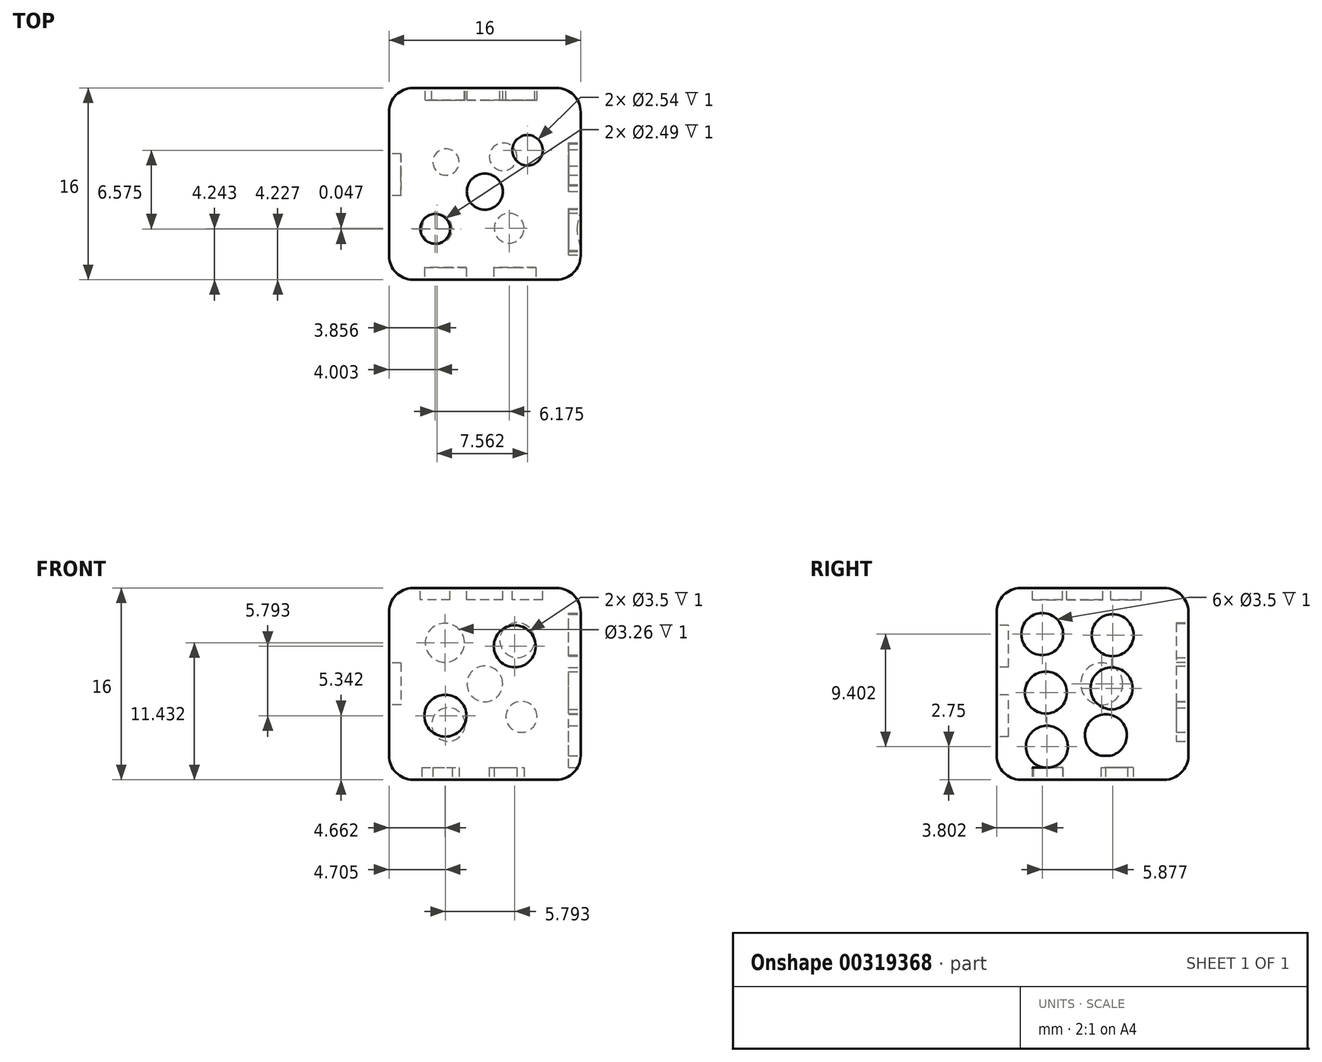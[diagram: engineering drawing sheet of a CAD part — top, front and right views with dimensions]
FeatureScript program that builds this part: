
annotation { "Feature Type Name" : "Feature", "Feature Type Description" : "" }
export const myFeature = defineFeature(function(context is Context, id is Id, definition is map)
    precondition{}
    {
        {
            var Q0;
            Q0=qCreatedBy(makeId("Front.planeOp"),FACE);
            var sketch = newSketch(context, id + "F0", { "sketchPlane" : qUnion([Q0])});
            skLineSegment(sketch, "E0.bottom", {"start": v(8, 8) * mm, "end": v(-8, 8) * mm});
            skLineSegment(sketch, "E0.top", {"start": v(8, -8) * mm, "end": v(-8, -8) * mm});
            skLineSegment(sketch, "E0.left", {"start": v(8, 8) * mm, "end": v(8, -8) * mm});
            skLineSegment(sketch, "E0.right", {"start": v(-8, 8) * mm, "end": v(-8, -8) * mm});
            skPoint(sketch, "E0.middle", {"position": v(0, 0) * mm});
            skSolve(sketch);
        }
        {
            var Q0;
            Q0 = qSketchRegion(id + "F0", true);
            extrude(context, id + "F1", {"entities" : qUnion([Q0]), "depth" : 16 * mm});
        }
        {
            var Q0;
            Q0=makeQuery(id+"F1.opExtrude","CAP_EDGE",EDGE,{"disambiguationData":[OSD([sQuery(id+"F0.wireOp",EDGE,"E0.left")])],"isStart":false});
            var Q1;
            Q1=makeQuery(id+"F1.opExtrude","CAP_EDGE",EDGE,{"disambiguationData":[OSD([sQuery(id+"F0.wireOp",EDGE,"E0.bottom")])],"isStart":false});
            var Q2;
            Q2=makeQuery(id+"F1.opExtrude","CAP_EDGE",EDGE,{"disambiguationData":[OSD([sQuery(id+"F0.wireOp",EDGE,"E0.top")])],"isStart":false});
            var Q3;
            Q3=makeQuery(id+"F1.opExtrude","CAP_EDGE",EDGE,{"disambiguationData":[OSD([sQuery(id+"F0.wireOp",EDGE,"E0.right")])],"isStart":false});
            var Q4;
            Q4=makeQuery(id+"F1.opExtrude","CAP_EDGE",EDGE,{"disambiguationData":[OSD([sQuery(id+"F0.wireOp",EDGE,"E0.right")])],"isStart":true});
            var Q5;
            Q5=makeQuery(id+"F1.opExtrude","SWEPT_EDGE",EDGE,{"disambiguationData":[OSD([sQuery(id+"F0.wireOp",EDGE,"E0.bottom"),sQuery(id+"F0.wireOp",EDGE,"E0.right")])]});
            var Q6;
            Q6=makeQuery(id+"F1.opExtrude","SWEPT_EDGE",EDGE,{"disambiguationData":[OSD([sQuery(id+"F0.wireOp",EDGE,"E0.top"),sQuery(id+"F0.wireOp",EDGE,"E0.right")])]});
            var Q7;
            Q7=makeQuery(id+"F1.opExtrude","SWEPT_FACE",FACE,{"disambiguationData":[OSD([sQuery(id+"F0.wireOp",EDGE,"E0.right")])]});
            var Q8;
            Q8=makeQuery(id+"F1.opExtrude","CAP_EDGE",EDGE,{"disambiguationData":[OSD([sQuery(id+"F0.wireOp",EDGE,"E0.bottom")])],"isStart":true});
            var Q9;
            Q9=makeQuery(id+"F1.opExtrude","SWEPT_EDGE",EDGE,{"disambiguationData":[OSD([sQuery(id+"F0.wireOp",EDGE,"E0.bottom"),sQuery(id+"F0.wireOp",EDGE,"E0.left")])]});
            var Q10;
            Q10=makeQuery(id+"F1.opExtrude","CAP_EDGE",EDGE,{"disambiguationData":[OSD([sQuery(id+"F0.wireOp",EDGE,"E0.left")])],"isStart":true});
            var Q11;
            Q11=makeQuery(id+"F1.opExtrude","CAP_EDGE",EDGE,{"disambiguationData":[OSD([sQuery(id+"F0.wireOp",EDGE,"E0.top")])],"isStart":true});
            var Q12;
            Q12=makeQuery(id+"F1.opExtrude","SWEPT_EDGE",EDGE,{"disambiguationData":[OSD([sQuery(id+"F0.wireOp",EDGE,"E0.top"),sQuery(id+"F0.wireOp",EDGE,"E0.left")])]});
            fillet(context, id + "F2", {"entities" : qUnion([Q0, Q1, Q2, Q3, Q4, Q5, Q6, Q7, Q8, Q9, Q10, Q11, Q12]), "radius" : 2 * mm, "tangentPropagation" : true, "allowEdgeOverflow" : false});
        }
        {
            var Q0;
            Q0=makeQuery(id+"F1.opExtrude","CAP_FACE",FACE,{"disambiguationData":[OSD([sQuery(id+"F0.wireOp",EDGE,"E0.bottom"),sQuery(id+"F0.wireOp",EDGE,"E0.top"),sQuery(id+"F0.wireOp",EDGE,"E0.left"),sQuery(id+"F0.wireOp",EDGE,"E0.right")])],"isStart":false});
            var sketch = newSketch(context, id + "F3", { "sketchPlane" : qUnion([Q0])});
            skCircle(sketch, "E1", {"center": v(-3.3, -2.66) * mm, "radius": 1.75 * mm});
            skCircle(sketch, "E2", {"center": v(2.5, 3.14) * mm, "radius": 1.75 * mm});
            skSolve(sketch);
        }
        {
            var Q0;
            Q0=makeQuery(id+"F1.opExtrude","SWEPT_FACE",FACE,{"disambiguationData":[OSD([sQuery(id+"F0.wireOp",EDGE,"E0.right")])]});
            var sketch = newSketch(context, id + "F4", { "sketchPlane" : qUnion([Q0])});
            skCircle(sketch, "E3", {"center": v(7.24, 0) * mm, "radius": 1.75 * mm});
            skPoint(sketch, "E3.centerSnap0", {"position": v(2, 0) * mm});
            skSolve(sketch);
        }
        {
            var Q0;
            Q0=makeQuery(id+"F1.opExtrude","CAP_FACE",FACE,{"disambiguationData":[OSD([sQuery(id+"F0.wireOp",EDGE,"E0.bottom"),sQuery(id+"F0.wireOp",EDGE,"E0.top"),sQuery(id+"F0.wireOp",EDGE,"E0.left"),sQuery(id+"F0.wireOp",EDGE,"E0.right")])],"isStart":true});
            var sketch = newSketch(context, id + "F5", { "sketchPlane" : qUnion([Q0])});
            skCircle(sketch, "E4", {"center": v(0, 0) * mm, "radius": 1.5 * mm});
            skCircle(sketch, "E5", {"center": v(3.05, -3.4) * mm, "radius": 1.4 * mm});
            skCircle(sketch, "E6", {"center": v(-2.7, 3.65) * mm, "radius": 1.46 * mm});
            skCircle(sketch, "E7", {"center": v(3.34, 3.43) * mm, "radius": 1.63 * mm});
            skCircle(sketch, "E8", {"center": v(-3.06, -2.75) * mm, "radius": 1.3 * mm});
            skSolve(sketch);
        }
        {
            var Q0;
            Q0=makeQuery(id+"F1.opExtrude","SWEPT_FACE",FACE,{"disambiguationData":[OSD([sQuery(id+"F0.wireOp",EDGE,"E0.bottom")])]});
            var sketch = newSketch(context, id + "F6", { "sketchPlane" : qUnion([Q0])});
            skCircle(sketch, "E9", {"center": v(-4.14, -11.76) * mm, "radius": 1.24 * mm});
            skCircle(sketch, "E10", {"center": v(0, -8.65) * mm, "radius": 1.5 * mm});
            skCircle(sketch, "E11", {"center": v(3.57, -5.2) * mm, "radius": 1.27 * mm});
            skSolve(sketch);
        }
        {
            var Q0;
            Q0=makeQuery(id+"F1.opExtrude","SWEPT_FACE",FACE,{"disambiguationData":[OSD([sQuery(id+"F0.wireOp",EDGE,"E0.left")])]});
            var sketch = newSketch(context, id + "F7", { "sketchPlane" : qUnion([Q0])});
            skCircle(sketch, "E12", {"center": v(-11.8, -5.25) * mm, "radius": 1.75 * mm});
            skCircle(sketch, "E13", {"center": v(-11.9, -0.72) * mm, "radius": 1.75 * mm});
            skCircle(sketch, "E14", {"center": v(-12.2, 4.15) * mm, "radius": 1.75 * mm});
            skCircle(sketch, "E15", {"center": v(-6.89, -4.3) * mm, "radius": 1.75 * mm});
            skCircle(sketch, "E16", {"center": v(-6.4, -0.38) * mm, "radius": 1.75 * mm});
            skCircle(sketch, "E17", {"center": v(-6.32, 4.07) * mm, "radius": 1.75 * mm});
            skSolve(sketch);
        }
        {
            var Q0;
            Q0=makeQuery(id+"F1.opExtrude","SWEPT_FACE",FACE,{"disambiguationData":[OSD([sQuery(id+"F0.wireOp",EDGE,"E0.top")])]});
            var sketch = newSketch(context, id + "F8", { "sketchPlane" : qUnion([Q0])});
            skCircle(sketch, "E18", {"center": v(-4, 11.77) * mm, "radius": 1.27 * mm});
            skCircle(sketch, "E19", {"center": v(2.03, 11.71) * mm, "radius": 1.25 * mm});
            skCircle(sketch, "E20", {"center": v(-3.24, 6.18) * mm, "radius": 1.1 * mm});
            skCircle(sketch, "E21", {"center": v(1.53, 5.74) * mm, "radius": 1.15 * mm});
            skSolve(sketch);
        }
        {
            var Q0;
            Q0=makeQuery(id+"F7.imprint","IMPRINT",FACE,{"disambiguationData":[TD([[makeQuery(id+"F7.imprint","IMPRINT",EDGE,{"derivedFrom":sQuery(id+"F7.wireOp",EDGE,"E13")}),1.0]])]});
            var Q1;
            Q1=makeQuery(id+"F7.imprint","IMPRINT",FACE,{"disambiguationData":[TD([[makeQuery(id+"F7.imprint","IMPRINT",EDGE,{"derivedFrom":sQuery(id+"F7.wireOp",EDGE,"E16")}),1.0]])]});
            var Q2;
            {var subQ0=sQuery(id+"F7.wireOp",EDGE,"E15");var subQ1=sQuery(id+"F0.wireOp",EDGE,"E0.left");var subQ2=makeQuery(id+"F2.opFillet","BLEND_EDGE",EDGE,{"blendedFrom":[makeQuery(id+"F1.opExtrude","SWEPT_EDGE",EDGE,{"disambiguationData":[OSD([sQuery(id+"F0.wireOp",EDGE,"E0.top"),subQ1])]}),makeQuery(id+"F1.opExtrude","SWEPT_FACE",FACE,{"disambiguationData":[OSD([subQ1])]})],"blendedInto":[makeQuery(id+"F1.opExtrude","SWEPT_FACE",FACE,{"disambiguationData":[OSD([subQ1])]})]});var subQ3=makeQuery(id+"F7.imprint","INTERSECT",VERTEX,{"disambiguationData":[OD(0.0)],"derivedFrom":[subQ2,subQ0]});Q2=makeQuery(id+"F7.imprint","IMPRINT",FACE,{"disambiguationData":[TD([[makeQuery(id+"F7.imprint","IMPRINT",EDGE,{"disambiguationData":[TD([[subQ3,-1.0]])],"derivedFrom":subQ0}),1.0]])]});}
            var Q3;
            Q3=makeQuery(id+"F7.imprint","IMPRINT",FACE,{"disambiguationData":[TD([[makeQuery(id+"F7.imprint","IMPRINT",EDGE,{"derivedFrom":sQuery(id+"F7.wireOp",EDGE,"E12")}),1.0]])]});
            var Q4;
            Q4=makeQuery(id+"F7.imprint","IMPRINT",FACE,{"disambiguationData":[TD([[makeQuery(id+"F7.imprint","IMPRINT",EDGE,{"derivedFrom":sQuery(id+"F7.wireOp",EDGE,"E17")}),1.0]])]});
            var Q5;
            Q5=makeQuery(id+"F7.imprint","IMPRINT",FACE,{"disambiguationData":[TD([[makeQuery(id+"F7.imprint","IMPRINT",EDGE,{"derivedFrom":sQuery(id+"F7.wireOp",EDGE,"E14")}),1.0]])]});
            extrude(context, id + "F9", {"entities" : qUnion([Q0, Q1, Q2, Q3, Q4, Q5]), "operationType" : NewBodyOperationType.REMOVE, "oppositeDirection" : true, "depth" : 1 * mm});
        }
        {
            var Q0;
            Q0 = qSketchRegion(id + "F5", true);
            extrude(context, id + "F10", {"entities" : qUnion([Q0]), "operationType" : NewBodyOperationType.REMOVE, "oppositeDirection" : true, "depth" : 1 * mm});
        }
        {
            var Q0;
            Q0 = qSketchRegion(id + "F4", true);
            extrude(context, id + "F11", {"entities" : qUnion([Q0]), "operationType" : NewBodyOperationType.REMOVE, "oppositeDirection" : true, "depth" : 1 * mm});
        }
        {
            var Q0;
            Q0 = qSketchRegion(id + "F3", true);
            extrude(context, id + "F12", {"entities" : qUnion([Q0]), "operationType" : NewBodyOperationType.REMOVE, "oppositeDirection" : true, "depth" : 1 * mm});
        }
        {
            var Q0;
            Q0 = qSketchRegion(id + "F8", true);
            extrude(context, id + "F13", {"entities" : qUnion([Q0]), "operationType" : NewBodyOperationType.REMOVE, "oppositeDirection" : true, "depth" : 1 * mm});
        }
        {
            var Q0;
            Q0 = qSketchRegion(id + "F6", true);
            extrude(context, id + "F14", {"entities" : qUnion([Q0]), "operationType" : NewBodyOperationType.REMOVE, "oppositeDirection" : true, "depth" : 1 * mm});
        }
    });
